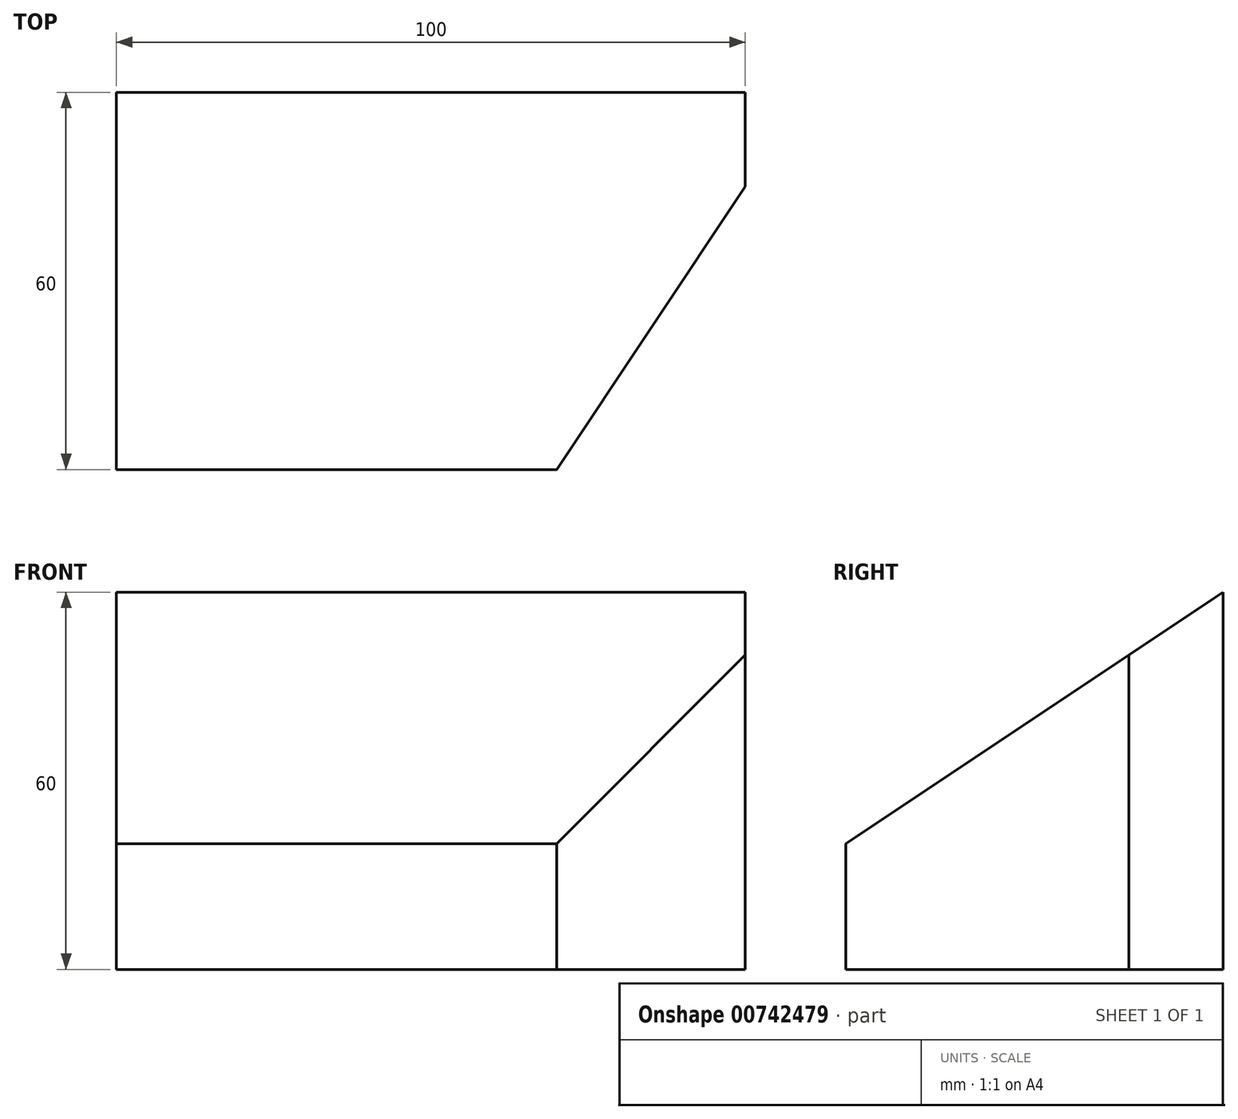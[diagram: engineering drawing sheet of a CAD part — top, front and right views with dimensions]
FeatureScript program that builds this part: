
annotation { "Feature Type Name" : "Feature", "Feature Type Description" : "" }
export const myFeature = defineFeature(function(context is Context, id is Id, definition is map)
    precondition{}
    {
        {
            var Q0;
            Q0=qCreatedBy(makeId("Front.planeOp"),FACE);
            var sketch = newSketch(context, id + "F0", { "sketchPlane" : qUnion([Q0])});
            skLineSegment(sketch, "E0.bottom", {"start": v(0, 0) * mm, "end": v(100, 0) * mm});
            skLineSegment(sketch, "E0.top", {"start": v(0, 60) * mm, "end": v(100, 60) * mm});
            skLineSegment(sketch, "E0.left", {"start": v(0, 0) * mm, "end": v(0, 60) * mm});
            skLineSegment(sketch, "E0.right", {"start": v(100, 0) * mm, "end": v(100, 60) * mm});
            skSolve(sketch);
        }
        {
            var Q0;
            {var subQ4=sQuery(id+"F0.wireOp",EDGE,"vdm43fAp-b9IH-N9Os-27JY-H0rcSxCsE5Zx");Q0=makeQuery(id+"F0.imprint","IMPRINT",FACE,{"disambiguationData":[TD([[makeQuery(id+"F0.imprint","IMPRINT",EDGE,{"derivedFrom":subQ4}),-1.0]])]});}
            var Q1;
            {var subQ2=sQuery(id+"F0.wireOp",EDGE,"E0.top");Q1=makeQuery(id+"F0.imprint","IMPRINT",FACE,{"disambiguationData":[TD([[makeQuery(id+"F0.imprint","IMPRINT",EDGE,{"derivedFrom":subQ2}),-1.0]])]});}
            extrude(context, id + "F1", {"entities" : qUnion([Q0, Q1]), "depth" : 60 * mm, "offsetDistance" : 25 * mm});
        }
        {
            var Q0;
            Q0=makeQuery(id+"F1.opExtrude","SWEPT_FACE",FACE,{"disambiguationData":[OSD([sQuery(id+"F0.wireOp",EDGE,"E0.left")])]});
            var sketch = newSketch(context, id + "F2", { "sketchPlane" : qUnion([Q0])});
            skLineSegment(sketch, "E1", {"start": v(0, 60) * mm, "end": v(60, 20) * mm});
            skSolve(sketch);
        }
        {
            var Q0;
            Q0=makeQuery(id+"F1.opExtrude","SWEPT_FACE",FACE,{"disambiguationData":[OSD([sQuery(id+"F0.wireOp",EDGE,"E0.top")])]});
            var sketch = newSketch(context, id + "F3", { "sketchPlane" : qUnion([Q0])});
            skLineSegment(sketch, "E2", {"start": v(100, -15) * mm, "end": v(70, -60) * mm});
            skSolve(sketch);
        }
        {
            var Q0;
            {var subQ0=sQuery(id+"F3.wireOp",EDGE,"E2");Q0=makeQuery(id+"F3.imprint","IMPRINT",FACE,{"disambiguationData":[TD([[makeQuery(id+"F3.imprint","IMPRINT",EDGE,{"derivedFrom":subQ0}),1.0]])]});}
            extrude(context, id + "F4", {"entities" : qUnion([Q0]), "operationType" : NewBodyOperationType.REMOVE, "endBound" : BoundingType.THROUGH_ALL, "oppositeDirection" : true, "depth" : 25 * mm, "offsetDistance" : 25 * mm});
        }
        {
            var Q0;
            {var subQ0=sQuery(id+"F2.wireOp",EDGE,"E1");Q0=makeQuery(id+"F2.imprint","IMPRINT",FACE,{"disambiguationData":[TD([[makeQuery(id+"F2.imprint","IMPRINT",EDGE,{"derivedFrom":subQ0}),1.0]])]});}
            extrude(context, id + "F5", {"entities" : qUnion([Q0]), "operationType" : NewBodyOperationType.REMOVE, "endBound" : BoundingType.THROUGH_ALL, "oppositeDirection" : true, "depth" : 25 * mm, "offsetDistance" : 25 * mm});
        }
    });
